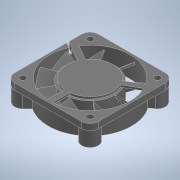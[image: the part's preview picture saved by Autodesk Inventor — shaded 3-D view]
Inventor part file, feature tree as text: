
AUTODESK INVENTOR PART (.ipt)
format: ipt  version: 2022 (Build 260153000, 153)  size: 339,968 bytes
history: imported  units: in
note: dims shown in document units (in); Inventor stores cm internally (conversion verified against a paired STEP export)
features: imported_body x1
ambient origin geometry x8: Origin, YZ Plane, XZ Plane, XY Plane, X Axis, Y Axis, Z Axis, Center Point
bodies: Solid1 (imported_parasolid), Body1 (imported_parasolid)
feature tree (1):
  imported_body  NMx_Import_Brep_tag  [imported B-rep: ~4 faces, bbox_mm=None]
